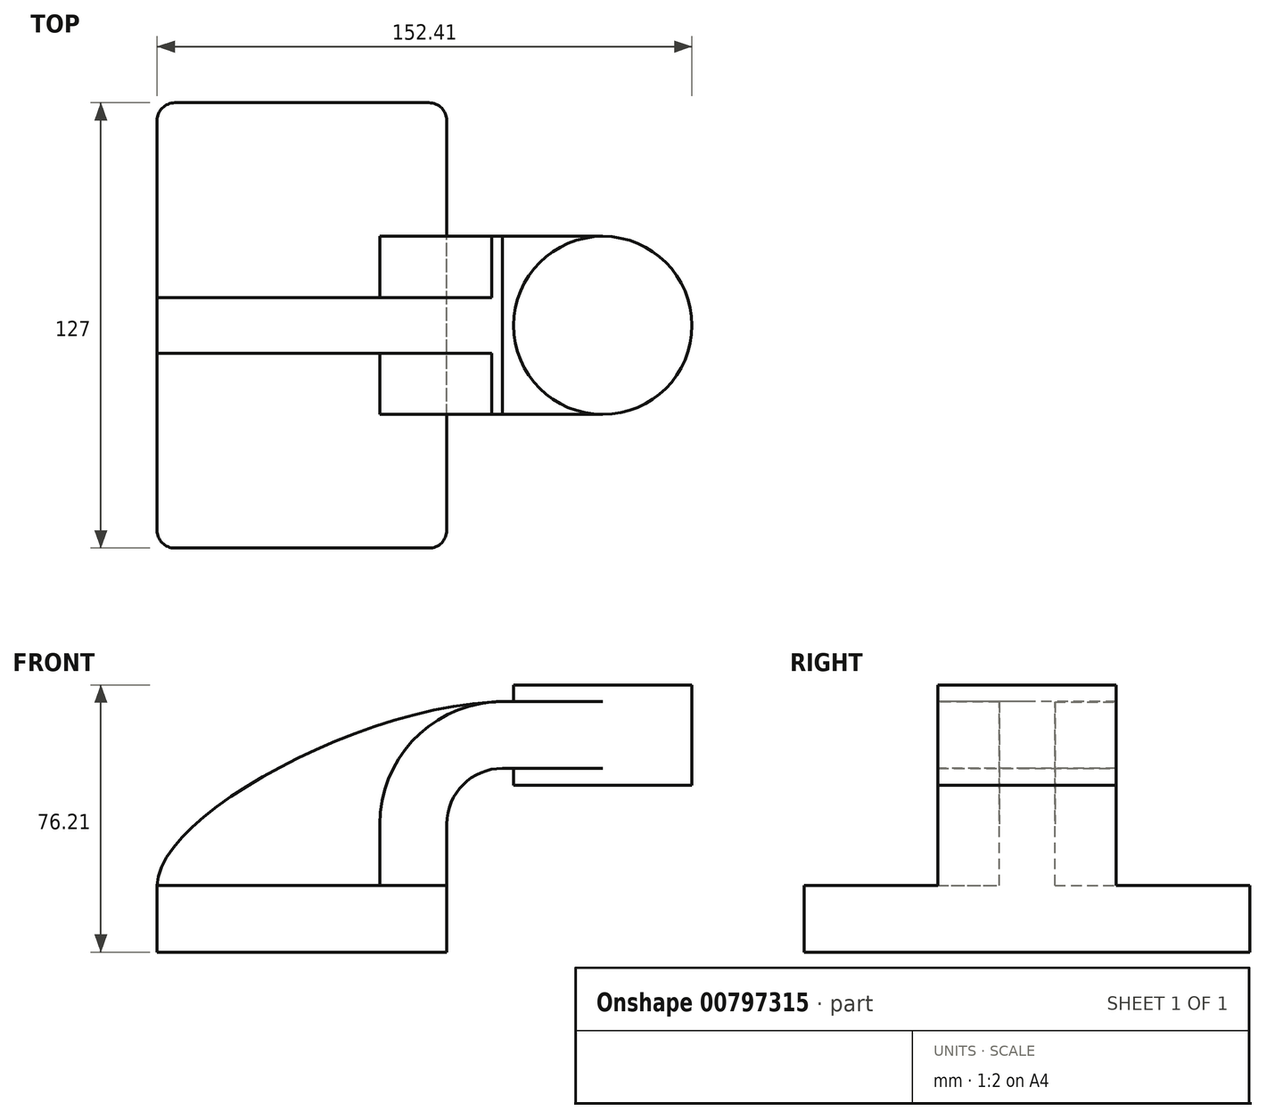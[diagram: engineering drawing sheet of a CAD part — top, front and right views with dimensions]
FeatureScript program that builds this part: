
annotation { "Feature Type Name" : "Feature", "Feature Type Description" : "" }
export const myFeature = defineFeature(function(context is Context, id is Id, definition is map)
    precondition{}
    {
        {
            var Q0;
            Q0=qCreatedBy(makeId("Front.planeOp"),FACE);
            var sketch = newSketch(context, id + "F0", { "sketchPlane" : qUnion([Q0])});
            skLineSegment(sketch, "E0.bottom", {"start": v(41.28, -9.52) * mm, "end": v(-41.27, -9.53) * mm});
            skLineSegment(sketch, "E0.top", {"start": v(41.27, 9.53) * mm, "end": v(-41.28, 9.53) * mm});
            skLineSegment(sketch, "E0.left", {"start": v(41.28, -9.52) * mm, "end": v(41.28, 9.53) * mm});
            skLineSegment(sketch, "E0.right", {"start": v(-41.27, -9.52) * mm, "end": v(-41.28, 9.53) * mm});
            skPoint(sketch, "E0.middle", {"position": v(0, 0) * mm});
            skLineSegment(sketch, "E1.bottom", {"start": v(111.12, 38.1) * mm, "end": v(60.32, 38.1) * mm});
            skLineSegment(sketch, "E1.top", {"start": v(111.12, 66.68) * mm, "end": v(60.32, 66.68) * mm});
            skLineSegment(sketch, "E1.left", {"start": v(111.12, 38.1) * mm, "end": v(111.12, 66.68) * mm});
            skLineSegment(sketch, "E1.right", {"start": v(60.32, 38.1) * mm, "end": v(60.32, 66.67) * mm});
            skPoint(sketch, "E1.middle", {"position": v(85.72, 52.39) * mm});
            skLineSegment(sketch, "E2", {"start": v(41.27, 9.53) * mm, "end": v(41.27, 27) * mm});
            skArc(sketch, "E3", {"start": v(41.27, 27) * mm, "mid": v(45.92, 38.23) * mm, "end": v(57.15, 42.88) * mm});
            skLineSegment(sketch, "E4", {"start": v(57.15, 42.88) * mm, "end": v(85.72, 42.88) * mm});
            skLineSegment(sketch, "E5.0", {"start": v(57.15, 61.93) * mm, "end": v(85.72, 61.93) * mm});
            skArc(sketch, "E5.1", {"start": v(22.23, 27) * mm, "mid": v(32.45, 51.7) * mm, "end": v(57.15, 61.93) * mm});
            skLineSegment(sketch, "E5.2", {"start": v(22.22, 9.53) * mm, "end": v(22.22, 27) * mm});
            skFitSpline(sketch, "E6", {"points": [v(-41.28, 9.52) * mm, v(57.15, 61.93) * mm], "startDerivative": vector(0.3, 58.5) * mm, "endDerivative": vector(122.37, 3.22) * mm});
            skLineSegment(sketch, "E7", {"start": v(85.72, 38.1) * mm, "end": v(85.72, 66.68) * mm});
            skSolve(sketch);
        }
        {
            var Q0;
            Q0=makeQuery(id+"F0.imprint","IMPRINT",FACE,{"disambiguationData":[TD([[makeQuery(id+"F0.imprint","IMPRINT",EDGE,{"derivedFrom":sQuery(id+"F0.wireOp",EDGE,"E0.bottom")}),-1.0]])]});
            extrude(context, id + "F1", {"entities" : qUnion([Q0]), "endBound" : BoundingType.SYMMETRIC, "depth" : 127 * mm, "offsetDistance" : 25.4 * mm});
        }
        {
            var Q0;
            {var subQ1=sQuery(id+"F0.wireOp",EDGE,"E2");Q0=makeQuery(id+"F0.imprint","IMPRINT",FACE,{"disambiguationData":[TD([[makeQuery(id+"F0.imprint","IMPRINT",EDGE,{"derivedFrom":subQ1}),1.0]])]});}
            var Q1;
            {var subQ0=sQuery(id+"F0.wireOp",EDGE,"E4");var subQ1=sQuery(id+"F0.wireOp",EDGE,"E1.right");var subQ2=makeQuery(id+"F0.imprint","INTERSECT",VERTEX,{"derivedFrom":[subQ1,subQ0]});Q1=makeQuery(id+"F0.imprint","IMPRINT",FACE,{"disambiguationData":[TD([[makeQuery(id+"F0.imprint","IMPRINT",EDGE,{"disambiguationData":[TD([[subQ2,-1.0]])],"derivedFrom":subQ1}),-1.0]])]});}
            extrude(context, id + "F2", {"entities" : qUnion([Q0, Q1]), "operationType" : NewBodyOperationType.ADD, "endBound" : BoundingType.SYMMETRIC, "depth" : 50.8 * mm, "offsetDistance" : 25.4 * mm});
        }
        {
            var Q0;
            {var subQ3=sQuery(id+"F0.wireOp",EDGE,"E5.2");Q0=makeQuery(id+"F0.imprint","IMPRINT",FACE,{"disambiguationData":[TD([[makeQuery(id+"F0.imprint","IMPRINT",EDGE,{"derivedFrom":subQ3}),1.0]])]});}
            extrude(context, id + "F3", {"entities" : qUnion([Q0]), "operationType" : NewBodyOperationType.ADD, "endBound" : BoundingType.SYMMETRIC, "depth" : 15.88 * mm, "offsetDistance" : 25.4 * mm});
        }
        {
            var Q0;
            {var subQ4=sQuery(id+"F0.wireOp",EDGE,"E1.left");Q0=makeQuery(id+"F0.imprint","IMPRINT",FACE,{"disambiguationData":[TD([[makeQuery(id+"F0.imprint","IMPRINT",EDGE,{"derivedFrom":subQ4}),1.0]])]});}
            var Q1;
            Q1=sQuery(id+"F0.wireOp",EDGE,"E7");
            revolve(context, id + "F4", {"operationType" : NewBodyOperationType.ADD, "surfaceOperationType" : NewSurfaceOperationType.NEW, "entities" : qUnion([Q0]), "axis" : qUnion([Q1]), "revolveType" : RevolveType.FULL});
        }
        {
            var Q0;
            Q0=makeQuery(id+"F1.opExtrude","CAP_EDGE",EDGE,{"disambiguationData":[OSD([sQuery(id+"F0.wireOp",EDGE,"E0.right")])],"isStart":false});
            var Q1;
            Q1=makeQuery(id+"F1.opExtrude","CAP_EDGE",EDGE,{"disambiguationData":[OSD([sQuery(id+"F0.wireOp",EDGE,"E0.left")])],"isStart":false});
            var Q2;
            Q2=makeQuery(id+"F1.opExtrude","CAP_EDGE",EDGE,{"disambiguationData":[OSD([sQuery(id+"F0.wireOp",EDGE,"E0.left")])],"isStart":true});
            var Q3;
            Q3=makeQuery(id+"F1.opExtrude","CAP_EDGE",EDGE,{"disambiguationData":[OSD([sQuery(id+"F0.wireOp",EDGE,"E0.right")])],"isStart":true});
            fillet(context, id + "F5", {"entities" : qUnion([Q0, Q1, Q2, Q3]), "radius" : 5.08 * mm, "tangentPropagation" : true, "allowEdgeOverflow" : false});
        }
    });
